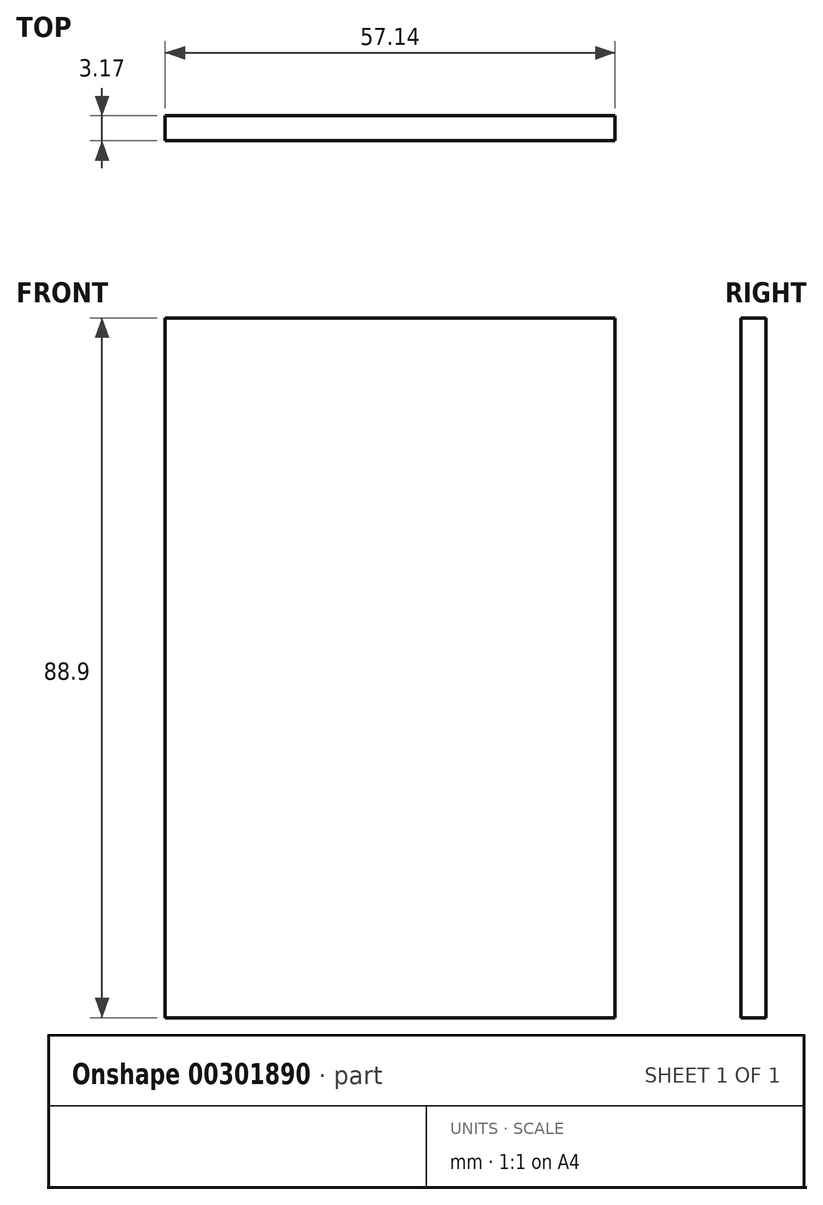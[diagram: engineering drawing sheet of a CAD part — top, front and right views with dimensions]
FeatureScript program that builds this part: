
annotation { "Feature Type Name" : "Feature", "Feature Type Description" : "" }
export const myFeature = defineFeature(function(context is Context, id is Id, definition is map)
    precondition{}
    {
        {
            var Q0;
            Q0=qCreatedBy(makeId("Front.planeOp"),FACE);
            var sketch = newSketch(context, id + "F0", { "sketchPlane" : qUnion([Q0])});
            skLineSegment(sketch, "E0.bottom", {"start": v(-28.57, 44.45) * mm, "end": v(28.58, 44.45) * mm});
            skLineSegment(sketch, "E0.top", {"start": v(-28.58, -44.45) * mm, "end": v(28.57, -44.45) * mm});
            skLineSegment(sketch, "E0.left", {"start": v(-28.57, 44.45) * mm, "end": v(-28.58, -44.45) * mm});
            skLineSegment(sketch, "E0.right", {"start": v(28.58, 44.45) * mm, "end": v(28.57, -44.45) * mm});
            skPoint(sketch, "E0.middle", {"position": v(0, 0) * mm});
            skSolve(sketch);
        }
        {
            var Q0;
            Q0 = qSketchRegion(id + "F0", true);
            extrude(context, id + "F1", {"entities" : qUnion([Q0]), "depth" : 3.17 * mm});
        }
    });
